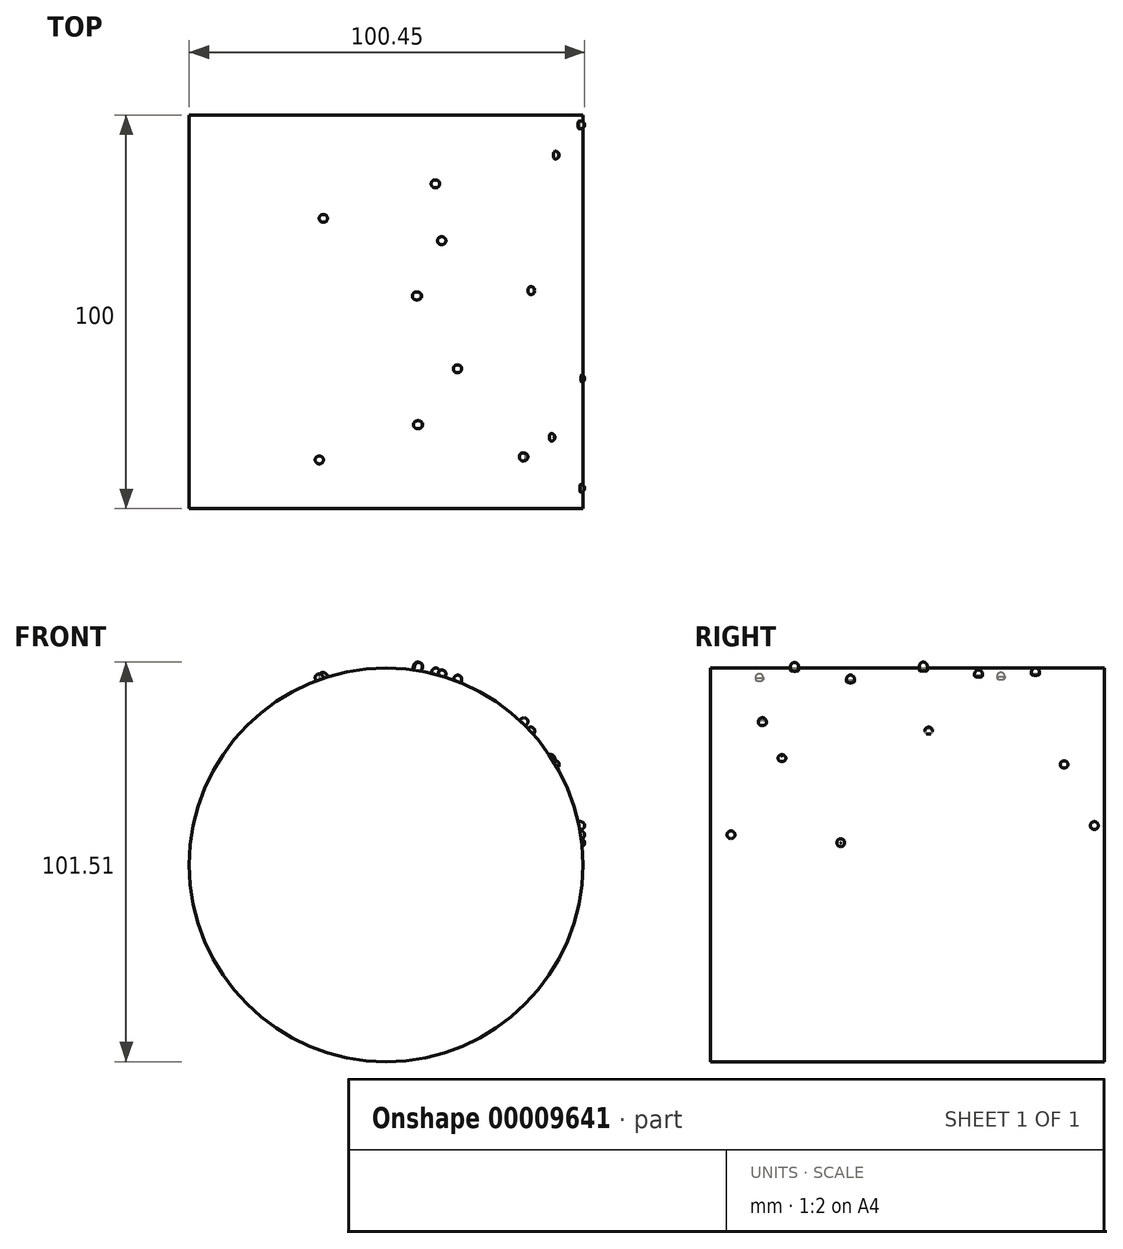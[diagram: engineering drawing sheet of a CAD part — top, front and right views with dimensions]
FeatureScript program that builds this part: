
annotation { "Feature Type Name" : "Feature", "Feature Type Description" : "" }
export const myFeature = defineFeature(function(context is Context, id is Id, definition is map)
    precondition{}
    {
        {
            var Q0;
            Q0=qCreatedBy(makeId("Front.planeOp"),FACE);
            var sketch = newSketch(context, id + "F0", { "sketchPlane" : qUnion([Q0])});
            skCircle(sketch, "E0.cCircle", {"center": v(0, 0) * mm, "radius": 45 * mm, "construction": true});
            skLineSegment(sketch, "E0.0", {"start": v(45, 14.62) * mm, "end": v(45, -14.62) * mm});
            skLineSegment(sketch, "E0.1", {"start": v(45, -14.62) * mm, "end": v(27.81, -38.28) * mm});
            skLineSegment(sketch, "E0.2", {"start": v(27.81, -38.28) * mm, "end": v(0, -47.32) * mm});
            skLineSegment(sketch, "E0.3", {"start": v(0, -47.32) * mm, "end": v(-27.81, -38.28) * mm});
            skLineSegment(sketch, "E0.4", {"start": v(-27.81, -38.28) * mm, "end": v(-45, -14.62) * mm});
            skLineSegment(sketch, "E0.5", {"start": v(-45, -14.62) * mm, "end": v(-45, 14.62) * mm});
            skLineSegment(sketch, "E0.6", {"start": v(-45, 14.62) * mm, "end": v(-27.81, 38.28) * mm});
            skLineSegment(sketch, "E0.7", {"start": v(-27.81, 38.28) * mm, "end": v(0, 47.32) * mm});
            skLineSegment(sketch, "E0.8", {"start": v(0, 47.32) * mm, "end": v(27.81, 38.28) * mm});
            skLineSegment(sketch, "E0.9", {"start": v(27.81, 38.28) * mm, "end": v(45, 14.62) * mm});
            skPoint(sketch, "E0.0.midPoint", {"position": v(45, 0) * mm});
            skSolve(sketch);
        }
        {
            var Q0;
            Q0=qSketchRegion(id+"F0",true);
            extrude(context, id + "F1", {"entities" : qUnion([Q0]), "endBound" : BoundingType.SYMMETRIC, "depth" : 100 * mm});
        }
        {
            var Q0;
            Q0=makeQuery(id+"F1.opExtrude","SWEPT_FACE",FACE,{"disambiguationData":[OSD([sQuery(id+"F0.wireOp",EDGE,"E0.8")])]});
            var sketch = newSketch(context, id + "F2", { "sketchPlane" : qUnion([Q0])});
            skCircle(sketch, "E1", {"center": v(-6.21, -28.67) * mm, "radius": 1 * mm});
            skCircle(sketch, "E2", {"center": v(4.22, -14.46) * mm, "radius": 1 * mm});
            skCircle(sketch, "E3", {"center": v(-6.5, 4.05) * mm, "radius": 1 * mm});
            skCircle(sketch, "E4", {"center": v(0, 18.08) * mm, "radius": 1 * mm});
            skCircle(sketch, "E5", {"center": v(-1.66, 32.53) * mm, "radius": 1 * mm});
            skSolve(sketch);
        }
        {
            var Q0;
            Q0=qSketchRegion(id+"F2",true);
            extrude(context, id + "F3", {"entities" : qUnion([Q0]), "operationType" : NewBodyOperationType.ADD, "depth" : 7 * mm});
        }
        {
            var Q0;
            Q0=makeQuery(id+"F1.opExtrude","SWEPT_FACE",FACE,{"disambiguationData":[OSD([sQuery(id+"F0.wireOp",EDGE,"E0.9")])]});
            var sketch = newSketch(context, id + "F4", { "sketchPlane" : qUnion([Q0])});
            skCircle(sketch, "E6", {"center": v(-36.85, 7.93) * mm, "radius": 1 * mm});
            skCircle(sketch, "E7", {"center": v(-31.88, -3.7) * mm, "radius": 1 * mm});
            skCircle(sketch, "E8", {"center": v(5.4, 4.97) * mm, "radius": 1 * mm});
            skCircle(sketch, "E9", {"center": v(39.8, -5.58) * mm, "radius": 1 * mm});
            skSolve(sketch);
        }
        {
            var Q0;
            Q0=qSketchRegion(id+"F4",true);
            extrude(context, id + "F5", {"entities" : qUnion([Q0]), "operationType" : NewBodyOperationType.ADD, "depth" : 7 * mm});
        }
        {
            var Q0;
            Q0=makeQuery(id+"F1.opExtrude","SWEPT_FACE",FACE,{"disambiguationData":[OSD([sQuery(id+"F0.wireOp",EDGE,"E0.7")])]});
            var sketch = newSketch(context, id + "F6", { "sketchPlane" : qUnion([Q0])});
            skCircle(sketch, "E10", {"center": v(1.06, 23.76) * mm, "radius": 1 * mm});
            skCircle(sketch, "E11", {"center": v(0, -37.62) * mm, "radius": 1 * mm});
            skSolve(sketch);
        }
        {
            var Q0;
            Q0=qSketchRegion(id+"F6",true);
            extrude(context, id + "F7", {"entities" : qUnion([Q0]), "operationType" : NewBodyOperationType.ADD, "depth" : 6 * mm});
        }
        {
            var Q0;
            Q0=makeQuery(id+"F1.opExtrude","SWEPT_FACE",FACE,{"disambiguationData":[OSD([sQuery(id+"F0.wireOp",EDGE,"E0.0")])]});
            var sketch = newSketch(context, id + "F8", { "sketchPlane" : qUnion([Q0])});
            skCircle(sketch, "E12", {"center": v(-16.94, 5.62) * mm, "radius": 1 * mm});
            skCircle(sketch, "E13", {"center": v(47.5, 9.98) * mm, "radius": 1 * mm});
            skCircle(sketch, "E14", {"center": v(-44.82, 7.65) * mm, "radius": 1 * mm});
            skSolve(sketch);
        }
        {
            var Q0;
            Q0=qSketchRegion(id+"F8",true);
            extrude(context, id + "F9", {"entities" : qUnion([Q0]), "operationType" : NewBodyOperationType.ADD, "depth" : 7 * mm});
        }
        {
            var Q0;
            Q0=qCreatedBy(makeId("Front.planeOp"),FACE);
            var sketch = newSketch(context, id + "F10", { "sketchPlane" : qUnion([Q0])});
            skCircle(sketch, "E15", {"center": v(1.55, 0) * mm, "radius": 50 * mm});
            skSolve(sketch);
        }
        {
            var Q0;
            Q0=qSketchRegion(id+"F10",true);
            extrude(context, id + "F11", {"entities" : qUnion([Q0]), "operationType" : NewBodyOperationType.ADD, "endBound" : BoundingType.SYMMETRIC, "depth" : 100 * mm});
        }
        {
            var Q0;
            Q0=makeQuery(id+"F7.opExtrude","CAP_EDGE",EDGE,{"disambiguationData":[OSD([sQuery(id+"F6.wireOp",EDGE,"E11")])],"isStart":false});
            var Q1;
            Q1=makeQuery(id+"F7.opExtrude","CAP_EDGE",EDGE,{"disambiguationData":[OSD([sQuery(id+"F6.wireOp",EDGE,"E10")])],"isStart":false});
            var Q2;
            Q2=makeQuery(id+"F3.opExtrude","CAP_EDGE",EDGE,{"disambiguationData":[OSD([sQuery(id+"F2.wireOp",EDGE,"E5")])],"isStart":false});
            var Q3;
            Q3=makeQuery(id+"F3.opExtrude","CAP_EDGE",EDGE,{"disambiguationData":[OSD([sQuery(id+"F2.wireOp",EDGE,"E4")])],"isStart":false});
            var Q4;
            Q4=makeQuery(id+"F3.opExtrude","CAP_EDGE",EDGE,{"disambiguationData":[OSD([sQuery(id+"F2.wireOp",EDGE,"E3")])],"isStart":false});
            var Q5;
            Q5=makeQuery(id+"F3.opExtrude","CAP_EDGE",EDGE,{"disambiguationData":[OSD([sQuery(id+"F2.wireOp",EDGE,"E2")])],"isStart":false});
            var Q6;
            Q6=makeQuery(id+"F3.opExtrude","CAP_EDGE",EDGE,{"disambiguationData":[OSD([sQuery(id+"F2.wireOp",EDGE,"E1")])],"isStart":false});
            var Q7;
            Q7=makeQuery(id+"F5.opExtrude","CAP_EDGE",EDGE,{"disambiguationData":[OSD([sQuery(id+"F4.wireOp",EDGE,"E6")])],"isStart":false});
            var Q8;
            Q8=makeQuery(id+"F5.opExtrude","CAP_EDGE",EDGE,{"disambiguationData":[OSD([sQuery(id+"F4.wireOp",EDGE,"E8")])],"isStart":false});
            var Q9;
            Q9=makeQuery(id+"F5.opExtrude","CAP_EDGE",EDGE,{"disambiguationData":[OSD([sQuery(id+"F4.wireOp",EDGE,"E9")])],"isStart":false});
            var Q10;
            Q10=makeQuery(id+"F5.opExtrude","CAP_EDGE",EDGE,{"disambiguationData":[OSD([sQuery(id+"F4.wireOp",EDGE,"E7")])],"isStart":false});
            var Q11;
            Q11=makeQuery(id+"F9.opExtrude","CAP_EDGE",EDGE,{"disambiguationData":[OSD([sQuery(id+"F8.wireOp",EDGE,"E14")])],"isStart":false});
            var Q12;
            Q12=makeQuery(id+"F9.opExtrude","CAP_EDGE",EDGE,{"disambiguationData":[OSD([sQuery(id+"F8.wireOp",EDGE,"E12")])],"isStart":false});
            var Q13;
            Q13=makeQuery(id+"F9.opExtrude","CAP_EDGE",EDGE,{"disambiguationData":[OSD([sQuery(id+"F8.wireOp",EDGE,"E13")])],"isStart":false});
            fillet(context, id + "F12", {"entities" : qUnion([Q0, Q1, Q2, Q3, Q4, Q5, Q6, Q7, Q8, Q9, Q10, Q11, Q12, Q13]), "radius" : 1 * mm, "tangentPropagation" : true, "allowEdgeOverflow" : false});
        }
    });
